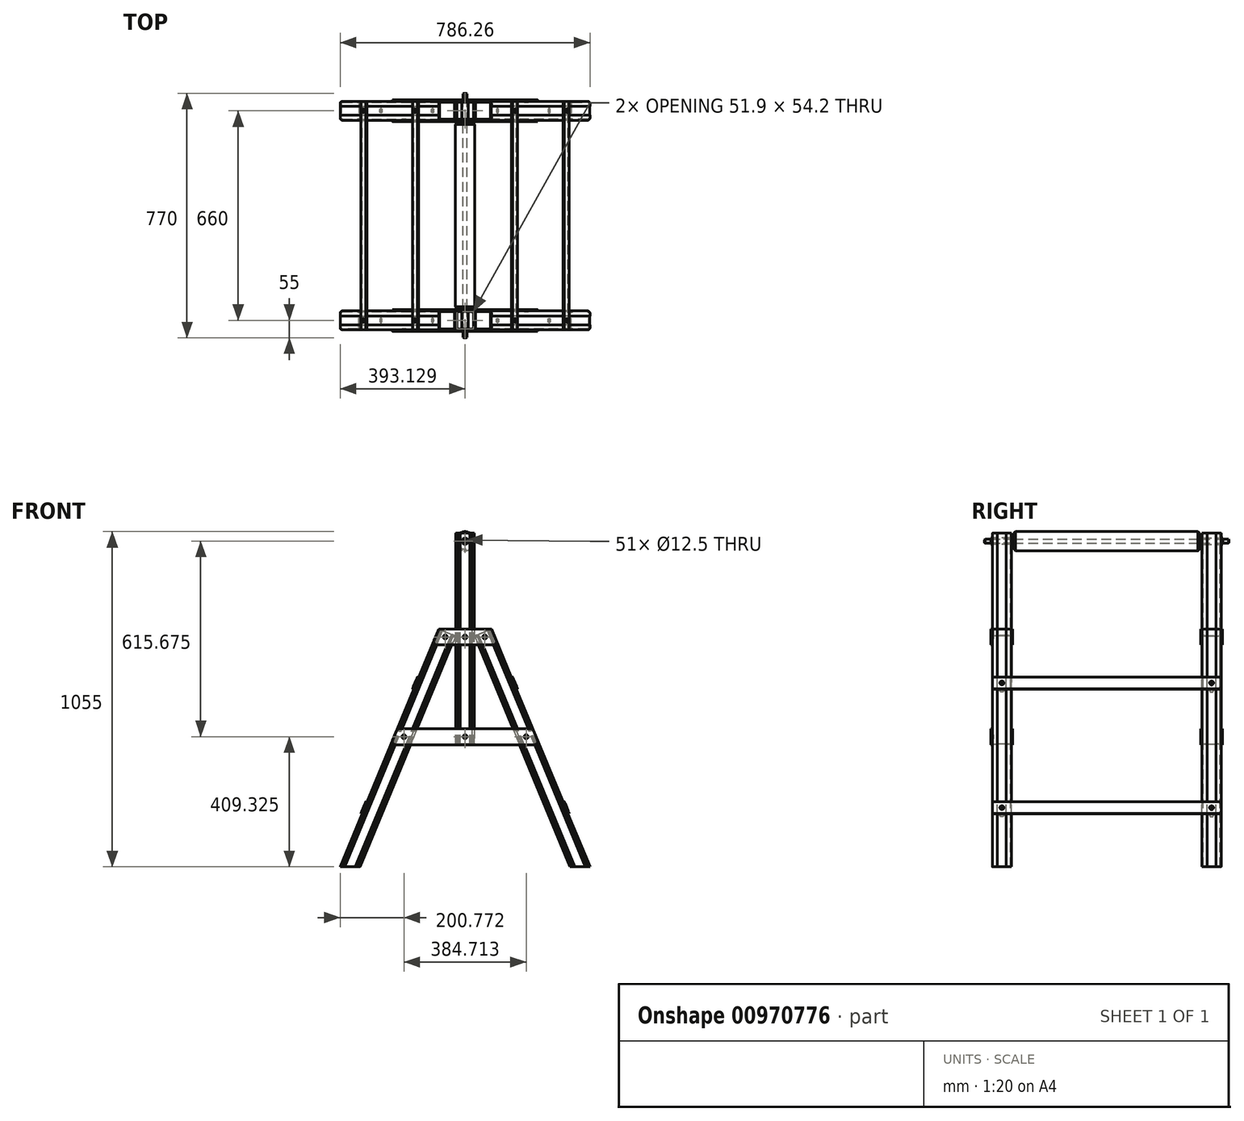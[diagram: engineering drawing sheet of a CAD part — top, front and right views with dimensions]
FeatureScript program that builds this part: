
annotation { "Feature Type Name" : "Feature", "Feature Type Description" : "" }
export const myFeature = defineFeature(function(context is Context, id is Id, definition is map)
    precondition{}
    {
        {
            var Q0;
            Q0=qCreatedBy(makeId("Front.planeOp"),FACE);
            var sketch = newSketch(context, id + "F0", { "sketchPlane" : qUnion([Q0])});
            skLineSegment(sketch, "E0", {"start": v(0, 0) * mm, "end": v(-309.97, 748.34) * mm});
            skLineSegment(sketch, "E1", {"start": v(-309.97, 748.34) * mm, "end": v(-363.28, 726.26) * mm});
            skLineSegment(sketch, "E2", {"start": v(-363.28, 726.26) * mm, "end": v(-62.45, 0) * mm});
            skLineSegment(sketch, "E3", {"start": v(-62.45, 0) * mm, "end": v(0, 0) * mm});
            skLineSegment(sketch, "E4", {"start": v(-336.63, 737.3) * mm, "end": v(-31.23, 0) * mm, "construction": true});
            skCircle(sketch, "E5", {"center": v(-330.89, 723.44) * mm, "radius": 6.25 * mm});
            skCircle(sketch, "E6", {"center": v(-200.77, 409.32) * mm, "radius": 6.25 * mm});
            skSolve(sketch);
        }
        {
            var Q0;
            Q0=qSketchRegion(id+"F0",true);
            extrude(context, id + "F1", {"entities" : qUnion([Q0]), "depth" : 60 * mm, "offsetDistance" : 25 * mm});
        }
        {
            var Q0;
            Q0=makeQuery(id+"F1.opExtrude","CAP_EDGE",EDGE,{"disambiguationData":[OSD([sQuery(id+"F0.wireOp",EDGE,"E0")])],"isStart":false});
            var Q1;
            Q1=makeQuery(id+"F1.opExtrude","CAP_EDGE",EDGE,{"disambiguationData":[OSD([sQuery(id+"F0.wireOp",EDGE,"E2")])],"isStart":false});
            var Q2;
            Q2=makeQuery(id+"F1.opExtrude","CAP_EDGE",EDGE,{"disambiguationData":[OSD([sQuery(id+"F0.wireOp",EDGE,"E0")])],"isStart":true});
            var Q3;
            Q3=makeQuery(id+"F1.opExtrude","CAP_EDGE",EDGE,{"disambiguationData":[OSD([sQuery(id+"F0.wireOp",EDGE,"E2")])],"isStart":true});
            fillet(context, id + "F2", {"entities" : qUnion([Q0, Q1, Q2, Q3]), "radius" : 7.5 * mm, "tangentPropagation" : true, "allowEdgeOverflow" : false});
        }
        {
            var Q0;
            Q0=makeQuery(id+"F1.opExtrude","SWEPT_FACE",FACE,{"disambiguationData":[OSD([sQuery(id+"F0.wireOp",EDGE,"E1")])]});
            var sketch = newSketch(context, id + "F3", { "sketchPlane" : qUnion([Q0])});
            skLineSegment(sketch, "E7", {"start": v(-50.2, -60) * mm, "end": v(-49.2, -59) * mm});
            skLineSegment(sketch, "E8", {"start": v(-49.2, -59) * mm, "end": v(-48.2, -60) * mm});
            skLineSegment(sketch, "E9", {"start": v(-48.2, -60) * mm, "end": v(-47.2, -59) * mm});
            skLineSegment(sketch, "E10", {"start": v(-47.2, -59) * mm, "end": v(-46.2, -60) * mm});
            skLineSegment(sketch, "E11", {"start": v(-46.2, -60) * mm, "end": v(-45.2, -59) * mm});
            skLineSegment(sketch, "E12", {"start": v(-45.2, -59) * mm, "end": v(-44.2, -60) * mm});
            skLineSegment(sketch, "E13", {"start": v(-28.85, -60) * mm, "end": v(-28.85, -30) * mm, "construction": true});
            skPoint(sketch, "E13.endSnap0", {"position": v(-57.7, -30) * mm});
            skLineSegment(sketch, "E14", {"start": v(-28.85, -30) * mm, "end": v(-57.7, -30) * mm, "construction": true});
            skLineSegment(sketch, "E15", {"start": v(-57.4, -44) * mm, "end": v(-57.7, -44) * mm});
            skLineSegment(sketch, "E16", {"start": v(-57.4, -44) * mm, "end": v(-57.4, -30) * mm});
            skArc(sketch, "E17.0", {"start": v(-54.8, -52.5) * mm, "mid": v(-53.45, -55.75) * mm, "end": v(-50.2, -57.1) * mm});
            skLineSegment(sketch, "E18", {"start": v(-54.8, -52.5) * mm, "end": v(-54.8, -30) * mm});
            skLineSegment(sketch, "E19", {"start": v(-50.2, -57.1) * mm, "end": v(-28.85, -57.1) * mm});
            skLineSegment(sketch, "E20.MirrorCS", {"start": v(-0.3, -44) * mm, "end": v(0, -44) * mm});
            skLineSegment(sketch, "E21.MirrorCS", {"start": v(-7.5, -60) * mm, "end": v(-8.5, -59) * mm});
            skLineSegment(sketch, "E22.MirrorCS", {"start": v(-11.5, -60) * mm, "end": v(-12.5, -59) * mm});
            skLineSegment(sketch, "E23.MirrorCS", {"start": v(-9.5, -60) * mm, "end": v(-10.5, -59) * mm});
            skLineSegment(sketch, "E24.MirrorCS", {"start": v(-12.5, -59) * mm, "end": v(-13.5, -60) * mm});
            skLineSegment(sketch, "E25.MirrorCS", {"start": v(-10.5, -59) * mm, "end": v(-11.5, -60) * mm});
            skLineSegment(sketch, "E26.MirrorCS", {"start": v(-8.5, -59) * mm, "end": v(-9.5, -60) * mm});
            skArc(sketch, "E27.MirrorCS", {"start": v(-2.9, -52.5) * mm, "mid": v(-4.25, -55.75) * mm, "end": v(-7.5, -57.1) * mm});
            skLineSegment(sketch, "E28.MirrorCS", {"start": v(-0.3, -44) * mm, "end": v(-0.3, -30) * mm});
            skLineSegment(sketch, "E29.MirrorCS", {"start": v(-7.5, -57.1) * mm, "end": v(-28.85, -57.1) * mm});
            skLineSegment(sketch, "E30.MirrorCS", {"start": v(-2.9, -52.5) * mm, "end": v(-2.9, -30) * mm});
            skLineSegment(sketch, "E31.MirrorCS", {"start": v(-50.2, 0) * mm, "end": v(-49.2, -1) * mm});
            skLineSegment(sketch, "E32.MirrorCS", {"start": v(-48.2, 0) * mm, "end": v(-47.2, -1) * mm});
            skLineSegment(sketch, "E33.MirrorCS", {"start": v(-49.2, -1) * mm, "end": v(-48.2, 0) * mm});
            skLineSegment(sketch, "E34.MirrorCS", {"start": v(-46.2, 0) * mm, "end": v(-45.2, -1) * mm});
            skLineSegment(sketch, "E35.MirrorCS", {"start": v(-47.2, -1) * mm, "end": v(-46.2, 0) * mm});
            skLineSegment(sketch, "E36.MirrorCS", {"start": v(-57.4, -16) * mm, "end": v(-57.7, -16) * mm});
            skLineSegment(sketch, "E37.MirrorCS", {"start": v(-45.2, -1) * mm, "end": v(-44.2, 0) * mm});
            skArc(sketch, "E38.MirrorCS", {"start": v(-54.8, -7.5) * mm, "mid": v(-53.45, -4.25) * mm, "end": v(-50.2, -2.9) * mm});
            skLineSegment(sketch, "E39.MirrorCS", {"start": v(-50.2, -2.9) * mm, "end": v(-28.85, -2.9) * mm});
            skLineSegment(sketch, "E40.MirrorCS", {"start": v(-54.8, -7.5) * mm, "end": v(-54.8, -30) * mm});
            skLineSegment(sketch, "E41.MirrorCS", {"start": v(-57.4, -16) * mm, "end": v(-57.4, -30) * mm});
            skLineSegment(sketch, "E42.MirrorCS", {"start": v(-9.5, 0) * mm, "end": v(-10.5, -1) * mm});
            skLineSegment(sketch, "E43.MirrorCS", {"start": v(-12.5, -1) * mm, "end": v(-13.5, 0) * mm});
            skLineSegment(sketch, "E44.MirrorCS", {"start": v(-10.5, -1) * mm, "end": v(-11.5, 0) * mm});
            skLineSegment(sketch, "E45.MirrorCS", {"start": v(-0.3, -16) * mm, "end": v(0, -16) * mm});
            skLineSegment(sketch, "E46.MirrorCS", {"start": v(-11.5, 0) * mm, "end": v(-12.5, -1) * mm});
            skLineSegment(sketch, "E47.MirrorCS", {"start": v(-7.5, 0) * mm, "end": v(-8.5, -1) * mm});
            skLineSegment(sketch, "E48.MirrorCS", {"start": v(-8.5, -1) * mm, "end": v(-9.5, 0) * mm});
            skLineSegment(sketch, "E49.MirrorCS", {"start": v(-2.9, -7.5) * mm, "end": v(-2.9, -30) * mm});
            skLineSegment(sketch, "E50.MirrorCS", {"start": v(-7.5, -2.9) * mm, "end": v(-28.85, -2.9) * mm});
            skArc(sketch, "E51.MirrorCS", {"start": v(-2.9, -7.5) * mm, "mid": v(-4.25, -4.25) * mm, "end": v(-7.5, -2.9) * mm});
            skLineSegment(sketch, "E52.MirrorCS", {"start": v(-0.3, -16) * mm, "end": v(-0.3, -30) * mm});
            skSolve(sketch);
        }
        {
            var Q0;
            Q0=makeQuery(id+"F3.imprint","IMPRINT",FACE,{"disambiguationData":[TD([[makeQuery(id+"F3.imprint","IMPRINT",EDGE,{"derivedFrom":sQuery(id+"F3.wireOp",EDGE,"E17.0")}),1.0]])]});
            var Q1;
            {var subQ0=sQuery(id+"F3.wireOp",EDGE,"E34.MirrorCS");Q1=makeQuery(id+"F3.imprint","IMPRINT",FACE,{"disambiguationData":[TD([[makeQuery(id+"F3.imprint","IMPRINT",EDGE,{"derivedFrom":subQ0}),1.0]])]});}
            var Q2;
            {var subQ0=sQuery(id+"F3.wireOp",EDGE,"E32.MirrorCS");Q2=makeQuery(id+"F3.imprint","IMPRINT",FACE,{"disambiguationData":[TD([[makeQuery(id+"F3.imprint","IMPRINT",EDGE,{"derivedFrom":subQ0}),1.0]])]});}
            var Q3;
            {var subQ0=sQuery(id+"F3.wireOp",EDGE,"E31.MirrorCS");Q3=makeQuery(id+"F3.imprint","IMPRINT",FACE,{"disambiguationData":[TD([[makeQuery(id+"F3.imprint","IMPRINT",EDGE,{"derivedFrom":subQ0}),1.0]])]});}
            var Q4;
            {var subQ1=sQuery(id+"F3.wireOp",EDGE,"E15");Q4=makeQuery(id+"F3.imprint","IMPRINT",FACE,{"disambiguationData":[TD([[makeQuery(id+"F3.imprint","IMPRINT",EDGE,{"derivedFrom":subQ1}),-1.0]])]});}
            var Q5;
            {var subQ0=sQuery(id+"F3.wireOp",EDGE,"E7");Q5=makeQuery(id+"F3.imprint","IMPRINT",FACE,{"disambiguationData":[TD([[makeQuery(id+"F3.imprint","IMPRINT",EDGE,{"derivedFrom":subQ0}),-1.0]])]});}
            var Q6;
            {var subQ0=sQuery(id+"F3.wireOp",EDGE,"E9");Q6=makeQuery(id+"F3.imprint","IMPRINT",FACE,{"disambiguationData":[TD([[makeQuery(id+"F3.imprint","IMPRINT",EDGE,{"derivedFrom":subQ0}),-1.0]])]});}
            var Q7;
            {var subQ0=sQuery(id+"F3.wireOp",EDGE,"E11");Q7=makeQuery(id+"F3.imprint","IMPRINT",FACE,{"disambiguationData":[TD([[makeQuery(id+"F3.imprint","IMPRINT",EDGE,{"derivedFrom":subQ0}),-1.0]])]});}
            var Q8;
            {var subQ0=sQuery(id+"F3.wireOp",EDGE,"E21.MirrorCS");Q8=makeQuery(id+"F3.imprint","IMPRINT",FACE,{"disambiguationData":[TD([[makeQuery(id+"F3.imprint","IMPRINT",EDGE,{"derivedFrom":subQ0}),1.0]])]});}
            var Q9;
            {var subQ0=sQuery(id+"F3.wireOp",EDGE,"E23.MirrorCS");Q9=makeQuery(id+"F3.imprint","IMPRINT",FACE,{"disambiguationData":[TD([[makeQuery(id+"F3.imprint","IMPRINT",EDGE,{"derivedFrom":subQ0}),1.0]])]});}
            var Q10;
            {var subQ0=sQuery(id+"F3.wireOp",EDGE,"E22.MirrorCS");Q10=makeQuery(id+"F3.imprint","IMPRINT",FACE,{"disambiguationData":[TD([[makeQuery(id+"F3.imprint","IMPRINT",EDGE,{"derivedFrom":subQ0}),1.0]])]});}
            var Q11;
            {var subQ1=sQuery(id+"F3.wireOp",EDGE,"E20.MirrorCS");Q11=makeQuery(id+"F3.imprint","IMPRINT",FACE,{"disambiguationData":[TD([[makeQuery(id+"F3.imprint","IMPRINT",EDGE,{"derivedFrom":subQ1}),1.0]])]});}
            var Q12;
            {var subQ0=sQuery(id+"F3.wireOp",EDGE,"E47.MirrorCS");Q12=makeQuery(id+"F3.imprint","IMPRINT",FACE,{"disambiguationData":[TD([[makeQuery(id+"F3.imprint","IMPRINT",EDGE,{"derivedFrom":subQ0}),-1.0]])]});}
            var Q13;
            {var subQ0=sQuery(id+"F3.wireOp",EDGE,"E42.MirrorCS");Q13=makeQuery(id+"F3.imprint","IMPRINT",FACE,{"disambiguationData":[TD([[makeQuery(id+"F3.imprint","IMPRINT",EDGE,{"derivedFrom":subQ0}),-1.0]])]});}
            var Q14;
            {var subQ0=sQuery(id+"F3.wireOp",EDGE,"E43.MirrorCS");Q14=makeQuery(id+"F3.imprint","IMPRINT",FACE,{"disambiguationData":[TD([[makeQuery(id+"F3.imprint","IMPRINT",EDGE,{"derivedFrom":subQ0}),-1.0]])]});}
            var Q15;
            Q15=makeQuery(id+"F1.opExtrude","SWEPT_FACE",FACE,{"disambiguationData":[OSD([sQuery(id+"F0.wireOp",EDGE,"E3")])]});
            extrude(context, id + "F4", {"entities" : qUnion([Q0, Q1, Q2, Q3, Q4, Q5, Q6, Q7, Q8, Q9, Q10, Q11, Q12, Q13, Q14]), "operationType" : NewBodyOperationType.REMOVE, "endBound" : BoundingType.UP_TO_SURFACE, "oppositeDirection" : true, "depth" : 25 * mm, "endBoundEntityFace" : qUnion([Q15]), "offsetDistance" : 25 * mm});
        }
        {
            var Q0;
            {var subQ0=sQuery(id+"F0.wireOp",EDGE,"E0");Q0=makeQuery(id+"F4.boolean.opBoolean","SPLIT",FACE,{"disambiguationData":[TD([makeQuery(id+"F4.opExtrude","SWEPT_FACE",FACE,{"disambiguationData":[OSD([sQuery(id+"F3.wireOp",EDGE,"E20.MirrorCS")])]})])],"derivedFrom":makeQuery(id+"F1.opExtrude","SWEPT_FACE",FACE,{"disambiguationData":[OSD([subQ0])]})});}
            var sketch = newSketch(context, id + "F5", { "sketchPlane" : qUnion([Q0])});
            skLineSegment(sketch, "E53", {"start": v(-60, 0) * mm, "end": v(0, 0) * mm, "construction": true});
            skLineSegment(sketch, "E54", {"start": v(-30, 0) * mm, "end": v(-30, 810) * mm, "construction": true});
            skCircle(sketch, "E55", {"center": v(-30, 200) * mm, "radius": 6.25 * mm});
            skCircle(sketch, "E56", {"center": v(-30, 625) * mm, "radius": 6.25 * mm});
            skSolve(sketch);
        }
        {
            var Q0;
            Q0=qSketchRegion(id+"F5",true);
            var Q1;
            {var subQ0=sQuery(id+"F0.wireOp",EDGE,"E2");Q1=makeQuery(id+"F4.boolean.opBoolean","SPLIT",FACE,{"disambiguationData":[TD([makeQuery(id+"F4.opExtrude","SWEPT_FACE",FACE,{"disambiguationData":[OSD([sQuery(id+"F3.wireOp",EDGE,"E15")])]})])],"derivedFrom":makeQuery(id+"F1.opExtrude","SWEPT_FACE",FACE,{"disambiguationData":[OSD([subQ0])]})});}
            extrude(context, id + "F6", {"entities" : qUnion([Q0]), "operationType" : NewBodyOperationType.REMOVE, "endBound" : BoundingType.UP_TO_SURFACE, "oppositeDirection" : true, "depth" : 25 * mm, "endBoundEntityFace" : qUnion([Q1]), "offsetDistance" : 25 * mm});
        }
        {
            var Q0;
            Q0=makeQuery(id+"F1.opExtrude","CAP_FACE",FACE,{"disambiguationData":[OSD([sQuery(id+"F0.wireOp",EDGE,"E0"),sQuery(id+"F0.wireOp",EDGE,"E1"),sQuery(id+"F0.wireOp",EDGE,"E2"),sQuery(id+"F0.wireOp",EDGE,"E3")])],"isStart":false});
            var sketch = newSketch(context, id + "F7", { "sketchPlane" : qUnion([Q0])});
            skLineSegment(sketch, "E57", {"start": v(-364.28, 1050) * mm, "end": v(-364.28, 386) * mm});
            skLineSegment(sketch, "E58", {"start": v(-364.28, 386) * mm, "end": v(-421.98, 386) * mm});
            skLineSegment(sketch, "E59", {"start": v(-421.98, 386) * mm, "end": v(-421.98, 1050) * mm});
            skLineSegment(sketch, "E60", {"start": v(-421.98, 1050) * mm, "end": v(-364.28, 1050) * mm});
            skLineSegment(sketch, "E61", {"start": v(-393.13, 386) * mm, "end": v(-393.13, 1050) * mm, "construction": true});
            skCircle(sketch, "E62", {"center": v(-393.13, 723.44) * mm, "radius": 6.25 * mm});
            skCircle(sketch, "E63", {"center": v(-393.13, 409.32) * mm, "radius": 6.25 * mm});
            skCircle(sketch, "E64", {"center": v(-393.13, 1025) * mm, "radius": 10 * mm});
            skLineSegment(sketch, "E65", {"start": v(-569.02, 403.07) * mm, "end": v(-237.44, 403.07) * mm, "construction": true});
            skLineSegment(sketch, "E66", {"start": v(-572.05, 717.2) * mm, "end": v(-0.55, 717.2) * mm, "construction": true});
            skSolve(sketch);
        }
        {
            var Q0;
            Q0=qSketchRegion(id+"F7",true);
            extrude(context, id + "F8", {"entities" : qUnion([Q0]), "oppositeDirection" : true, "depth" : 60 * mm, "offsetDistance" : 25 * mm});
        }
        {
            var Q0;
            Q0=makeQuery(id+"F8.opExtrude","CAP_EDGE",EDGE,{"disambiguationData":[OSD([sQuery(id+"F7.wireOp",EDGE,"E59")])],"isStart":true});
            var Q1;
            Q1=makeQuery(id+"F8.opExtrude","CAP_EDGE",EDGE,{"disambiguationData":[OSD([sQuery(id+"F7.wireOp",EDGE,"E57")])],"isStart":true});
            var Q2;
            Q2=makeQuery(id+"F8.opExtrude","CAP_EDGE",EDGE,{"disambiguationData":[OSD([sQuery(id+"F7.wireOp",EDGE,"E57")])],"isStart":false});
            var Q3;
            Q3=makeQuery(id+"F8.opExtrude","CAP_EDGE",EDGE,{"disambiguationData":[OSD([sQuery(id+"F7.wireOp",EDGE,"E59")])],"isStart":false});
            fillet(context, id + "F9", {"entities" : qUnion([Q0, Q1, Q2, Q3]), "radius" : 7.5 * mm, "tangentPropagation" : true, "allowEdgeOverflow" : false});
        }
        {
            var Q0;
            Q0=makeQuery(id+"F8.opExtrude","SWEPT_FACE",FACE,{"disambiguationData":[OSD([sQuery(id+"F7.wireOp",EDGE,"E60")])]});
            var sketch = newSketch(context, id + "F10", { "sketchPlane" : qUnion([Q0])});
            skLineSegment(sketch, "E67", {"start": v(-421.98, -30) * mm, "end": v(-393.13, -30) * mm, "construction": true});
            skPoint(sketch, "E67.endSnap0", {"position": v(-393.13, -60) * mm});
            skLineSegment(sketch, "E68", {"start": v(-393.13, -30) * mm, "end": v(-393.13, -60) * mm, "construction": true});
            skLineSegment(sketch, "E69", {"start": v(-414.48, -60) * mm, "end": v(-413.48, -59) * mm});
            skLineSegment(sketch, "E70", {"start": v(-413.48, -59) * mm, "end": v(-412.48, -60) * mm});
            skLineSegment(sketch, "E71", {"start": v(-421.68, -30) * mm, "end": v(-421.68, -44) * mm});
            skLineSegment(sketch, "E72", {"start": v(-421.68, -44) * mm, "end": v(-421.98, -44) * mm});
            skLineSegment(sketch, "E73", {"start": v(-412.48, -60) * mm, "end": v(-411.48, -59) * mm});
            skLineSegment(sketch, "E74", {"start": v(-411.48, -59) * mm, "end": v(-410.48, -60) * mm});
            skLineSegment(sketch, "E75", {"start": v(-410.48, -60) * mm, "end": v(-409.48, -59) * mm});
            skLineSegment(sketch, "E76", {"start": v(-409.48, -59) * mm, "end": v(-408.48, -60) * mm});
            skArc(sketch, "E77.0", {"start": v(-419.08, -52.5) * mm, "mid": v(-417.73, -55.75) * mm, "end": v(-414.48, -57.1) * mm});
            skLineSegment(sketch, "E78", {"start": v(-419.08, -52.5) * mm, "end": v(-419.08, -30) * mm});
            skLineSegment(sketch, "E79", {"start": v(-414.48, -57.1) * mm, "end": v(-393.13, -57.1) * mm});
            skLineSegment(sketch, "E80.MirrorCS", {"start": v(-364.58, -44) * mm, "end": v(-364.28, -44) * mm});
            skLineSegment(sketch, "E81.MirrorCS", {"start": v(-371.78, -60) * mm, "end": v(-372.78, -59) * mm});
            skLineSegment(sketch, "E82.MirrorCS", {"start": v(-372.78, -59) * mm, "end": v(-373.78, -60) * mm});
            skLineSegment(sketch, "E83.MirrorCS", {"start": v(-376.78, -59) * mm, "end": v(-377.78, -60) * mm});
            skLineSegment(sketch, "E84.MirrorCS", {"start": v(-373.78, -60) * mm, "end": v(-374.78, -59) * mm});
            skLineSegment(sketch, "E85.MirrorCS", {"start": v(-374.78, -59) * mm, "end": v(-375.78, -60) * mm});
            skLineSegment(sketch, "E86.MirrorCS", {"start": v(-375.78, -60) * mm, "end": v(-376.78, -59) * mm});
            skArc(sketch, "E87.MirrorCS", {"start": v(-367.18, -52.5) * mm, "mid": v(-368.53, -55.75) * mm, "end": v(-371.78, -57.1) * mm});
            skLineSegment(sketch, "E88.MirrorCS", {"start": v(-364.58, -30) * mm, "end": v(-364.58, -44) * mm});
            skLineSegment(sketch, "E89.MirrorCS", {"start": v(-371.78, -57.1) * mm, "end": v(-393.13, -57.1) * mm});
            skLineSegment(sketch, "E90.MirrorCS", {"start": v(-367.18, -52.5) * mm, "end": v(-367.18, -30) * mm});
            skLineSegment(sketch, "E91.MirrorCS", {"start": v(-412.48, 0) * mm, "end": v(-411.48, -1) * mm});
            skLineSegment(sketch, "E92.MirrorCS", {"start": v(-414.48, 0) * mm, "end": v(-413.48, -1) * mm});
            skLineSegment(sketch, "E93.MirrorCS", {"start": v(-413.48, -1) * mm, "end": v(-412.48, 0) * mm});
            skLineSegment(sketch, "E94.MirrorCS", {"start": v(-411.48, -1) * mm, "end": v(-410.48, 0) * mm});
            skLineSegment(sketch, "E95.MirrorCS", {"start": v(-421.68, -16) * mm, "end": v(-421.98, -16) * mm});
            skLineSegment(sketch, "E96.MirrorCS", {"start": v(-410.48, 0) * mm, "end": v(-409.48, -1) * mm});
            skLineSegment(sketch, "E97.MirrorCS", {"start": v(-409.48, -1) * mm, "end": v(-408.48, 0) * mm});
            skArc(sketch, "E98.MirrorCS", {"start": v(-419.08, -7.5) * mm, "mid": v(-417.73, -4.25) * mm, "end": v(-414.48, -2.9) * mm});
            skLineSegment(sketch, "E99.MirrorCS", {"start": v(-414.48, -2.9) * mm, "end": v(-393.13, -2.9) * mm});
            skLineSegment(sketch, "E100.MirrorCS", {"start": v(-419.08, -7.5) * mm, "end": v(-419.08, -30) * mm});
            skLineSegment(sketch, "E101.MirrorCS", {"start": v(-421.68, -30) * mm, "end": v(-421.68, -16) * mm});
            skLineSegment(sketch, "E102.MirrorCS", {"start": v(-374.78, -1) * mm, "end": v(-375.78, 0) * mm});
            skLineSegment(sketch, "E103.MirrorCS", {"start": v(-375.78, 0) * mm, "end": v(-376.78, -1) * mm});
            skLineSegment(sketch, "E104.MirrorCS", {"start": v(-371.78, 0) * mm, "end": v(-372.78, -1) * mm});
            skLineSegment(sketch, "E105.MirrorCS", {"start": v(-372.78, -1) * mm, "end": v(-373.78, 0) * mm});
            skLineSegment(sketch, "E106.MirrorCS", {"start": v(-373.78, 0) * mm, "end": v(-374.78, -1) * mm});
            skLineSegment(sketch, "E107.MirrorCS", {"start": v(-364.58, -16) * mm, "end": v(-364.28, -16) * mm});
            skLineSegment(sketch, "E108.MirrorCS", {"start": v(-376.78, -1) * mm, "end": v(-377.78, 0) * mm});
            skArc(sketch, "E109.MirrorCS", {"start": v(-367.18, -7.5) * mm, "mid": v(-368.53, -4.25) * mm, "end": v(-371.78, -2.9) * mm});
            skLineSegment(sketch, "E110.MirrorCS", {"start": v(-364.58, -30) * mm, "end": v(-364.58, -16) * mm});
            skLineSegment(sketch, "E111.MirrorCS", {"start": v(-367.18, -7.5) * mm, "end": v(-367.18, -30) * mm});
            skLineSegment(sketch, "E112.MirrorCS", {"start": v(-371.78, -2.9) * mm, "end": v(-393.13, -2.9) * mm});
            skSolve(sketch);
        }
        {
            var Q0;
            {var subQ0=sQuery(id+"F10.wireOp",EDGE,"E69");Q0=makeQuery(id+"F10.imprint","IMPRINT",FACE,{"disambiguationData":[TD([[makeQuery(id+"F10.imprint","IMPRINT",EDGE,{"derivedFrom":subQ0}),-1.0]])]});}
            var Q1;
            {var subQ0=sQuery(id+"F10.wireOp",EDGE,"E73");Q1=makeQuery(id+"F10.imprint","IMPRINT",FACE,{"disambiguationData":[TD([[makeQuery(id+"F10.imprint","IMPRINT",EDGE,{"derivedFrom":subQ0}),-1.0]])]});}
            var Q2;
            {var subQ0=sQuery(id+"F10.wireOp",EDGE,"E75");Q2=makeQuery(id+"F10.imprint","IMPRINT",FACE,{"disambiguationData":[TD([[makeQuery(id+"F10.imprint","IMPRINT",EDGE,{"derivedFrom":subQ0}),-1.0]])]});}
            var Q3;
            {var subQ0=sQuery(id+"F10.wireOp",EDGE,"E83.MirrorCS");Q3=makeQuery(id+"F10.imprint","IMPRINT",FACE,{"disambiguationData":[TD([[makeQuery(id+"F10.imprint","IMPRINT",EDGE,{"derivedFrom":subQ0}),1.0]])]});}
            var Q4;
            {var subQ0=sQuery(id+"F10.wireOp",EDGE,"E84.MirrorCS");Q4=makeQuery(id+"F10.imprint","IMPRINT",FACE,{"disambiguationData":[TD([[makeQuery(id+"F10.imprint","IMPRINT",EDGE,{"derivedFrom":subQ0}),1.0]])]});}
            var Q5;
            {var subQ0=sQuery(id+"F10.wireOp",EDGE,"E81.MirrorCS");Q5=makeQuery(id+"F10.imprint","IMPRINT",FACE,{"disambiguationData":[TD([[makeQuery(id+"F10.imprint","IMPRINT",EDGE,{"derivedFrom":subQ0}),1.0]])]});}
            var Q6;
            Q6=makeQuery(id+"F10.imprint","IMPRINT",FACE,{"disambiguationData":[TD([[makeQuery(id+"F10.imprint","IMPRINT",EDGE,{"derivedFrom":sQuery(id+"F10.wireOp",EDGE,"E71")}),-1.0]])]});
            var Q7;
            {var subQ1=sQuery(id+"F10.wireOp",EDGE,"E80.MirrorCS");Q7=makeQuery(id+"F10.imprint","IMPRINT",FACE,{"disambiguationData":[TD([[makeQuery(id+"F10.imprint","IMPRINT",EDGE,{"derivedFrom":subQ1}),1.0]])]});}
            var Q8;
            {var subQ0=sQuery(id+"F10.wireOp",EDGE,"E103.MirrorCS");Q8=makeQuery(id+"F10.imprint","IMPRINT",FACE,{"disambiguationData":[TD([[makeQuery(id+"F10.imprint","IMPRINT",EDGE,{"derivedFrom":subQ0}),-1.0]])]});}
            var Q9;
            {var subQ0=sQuery(id+"F10.wireOp",EDGE,"E102.MirrorCS");Q9=makeQuery(id+"F10.imprint","IMPRINT",FACE,{"disambiguationData":[TD([[makeQuery(id+"F10.imprint","IMPRINT",EDGE,{"derivedFrom":subQ0}),-1.0]])]});}
            var Q10;
            {var subQ0=sQuery(id+"F10.wireOp",EDGE,"E104.MirrorCS");Q10=makeQuery(id+"F10.imprint","IMPRINT",FACE,{"disambiguationData":[TD([[makeQuery(id+"F10.imprint","IMPRINT",EDGE,{"derivedFrom":subQ0}),-1.0]])]});}
            var Q11;
            {var subQ0=sQuery(id+"F10.wireOp",EDGE,"E92.MirrorCS");Q11=makeQuery(id+"F10.imprint","IMPRINT",FACE,{"disambiguationData":[TD([[makeQuery(id+"F10.imprint","IMPRINT",EDGE,{"derivedFrom":subQ0}),1.0]])]});}
            var Q12;
            {var subQ0=sQuery(id+"F10.wireOp",EDGE,"E91.MirrorCS");Q12=makeQuery(id+"F10.imprint","IMPRINT",FACE,{"disambiguationData":[TD([[makeQuery(id+"F10.imprint","IMPRINT",EDGE,{"derivedFrom":subQ0}),1.0]])]});}
            var Q13;
            {var subQ0=sQuery(id+"F10.wireOp",EDGE,"E96.MirrorCS");Q13=makeQuery(id+"F10.imprint","IMPRINT",FACE,{"disambiguationData":[TD([[makeQuery(id+"F10.imprint","IMPRINT",EDGE,{"derivedFrom":subQ0}),1.0]])]});}
            var Q14;
            Q14=makeQuery(id+"F10.imprint","IMPRINT",FACE,{"disambiguationData":[TD([[makeQuery(id+"F10.imprint","IMPRINT",EDGE,{"derivedFrom":sQuery(id+"F10.wireOp",EDGE,"E77.0")}),1.0]])]});
            var Q15;
            Q15=makeQuery(id+"F8.opExtrude","SWEPT_FACE",FACE,{"disambiguationData":[OSD([sQuery(id+"F7.wireOp",EDGE,"E58")])]});
            extrude(context, id + "F11", {"entities" : qUnion([Q0, Q1, Q2, Q3, Q4, Q5, Q6, Q7, Q8, Q9, Q10, Q11, Q12, Q13, Q14]), "operationType" : NewBodyOperationType.REMOVE, "endBound" : BoundingType.UP_TO_SURFACE, "oppositeDirection" : true, "depth" : 25 * mm, "endBoundEntityFace" : qUnion([Q15]), "offsetDistance" : 25 * mm});
        }
        {
            var Q0;
            Q0=makeQuery(id+"F11.boolean.opBoolean","COPY",FACE,{"derivedFrom":makeQuery(id+"F11.opExtrude","SWEPT_FACE",FACE,{"disambiguationData":[OSD([sQuery(id+"F10.wireOp",EDGE,"E88.MirrorCS"),sQuery(id+"F10.wireOp",EDGE,"E110.MirrorCS")])]})});
            var Q1;
            Q1=makeQuery(id+"F11.boolean.opBoolean","COPY",FACE,{"derivedFrom":makeQuery(id+"F11.opExtrude","SWEPT_FACE",FACE,{"disambiguationData":[OSD([sQuery(id+"F10.wireOp",EDGE,"E71"),sQuery(id+"F10.wireOp",EDGE,"E101.MirrorCS")])]})});
            cPlane(context, id + "F12", {"entities" : qUnion([Q0, Q1]), "cplaneType" : CPlaneType.MID_PLANE, "offset" : 25 * mm, "width" : 150 * mm, "height" : 150 * mm});
        }
        {
            var Q0;
            Q0=makeQuery(id+"F1.opExtrude","SWEPT_BODY",BODY,{"disambiguationData":[OSD([sQuery(id+"F0.wireOp",EDGE,"E0"),sQuery(id+"F0.wireOp",EDGE,"E1"),sQuery(id+"F0.wireOp",EDGE,"E2"),sQuery(id+"F0.wireOp",EDGE,"E3")])]});
            var Q1;
            Q1=qCreatedBy(id+"F12.planeOp",FACE);
            mirror(context, id + "F13", {"entities" : qUnion([Q0]), "mirrorPlane" : qUnion([Q1])});
        }
        {
            var Q0;
            Q0=makeQuery(id+"F13.opPattern","COPY",FACE,{"derivedFrom":makeQuery(id+"F1.opExtrude","CAP_FACE",FACE,{"disambiguationData":[OSD([sQuery(id+"F0.wireOp",EDGE,"E0"),sQuery(id+"F0.wireOp",EDGE,"E1"),sQuery(id+"F0.wireOp",EDGE,"E2"),sQuery(id+"F0.wireOp",EDGE,"E3")])],"isStart":false}),"instanceName":"1"});
            var sketch = newSketch(context, id + "F14", { "sketchPlane" : qUnion([Q0])});
            skCircle(sketch, "E113", {"center": v(-393.13, 723.44) * mm, "radius": 6.25 * mm});
            skCircle(sketch, "E114", {"center": v(-455.38, 723.44) * mm, "radius": 6.25 * mm});
            skCircle(sketch, "E115", {"center": v(-330.89, 723.44) * mm, "radius": 6.25 * mm});
            skLineSegment(sketch, "E116", {"start": v(-455.38, 723.44) * mm, "end": v(-330.89, 723.44) * mm, "construction": true});
            skLineSegment(sketch, "E117", {"start": v(-476.25, 748.44) * mm, "end": v(-496.96, 698.44) * mm});
            skLineSegment(sketch, "E118", {"start": v(-496.96, 698.44) * mm, "end": v(-289.3, 698.44) * mm});
            skLineSegment(sketch, "E119", {"start": v(-289.3, 698.44) * mm, "end": v(-310.02, 748.44) * mm});
            skLineSegment(sketch, "E120", {"start": v(-310.02, 748.44) * mm, "end": v(-476.25, 748.44) * mm});
            skLineSegment(sketch, "E121", {"start": v(-393.13, 723.44) * mm, "end": v(-393.13, 748.44) * mm, "construction": true});
            skLineSegment(sketch, "E122", {"start": v(-393.13, 723.44) * mm, "end": v(-393.13, 698.44) * mm, "construction": true});
            skCircle(sketch, "E123", {"center": v(-585.49, 409.32) * mm, "radius": 6.25 * mm});
            skCircle(sketch, "E124", {"center": v(-393.13, 409.32) * mm, "radius": 6.25 * mm});
            skCircle(sketch, "E125", {"center": v(-200.77, 409.32) * mm, "radius": 6.25 * mm});
            skLineSegment(sketch, "E126", {"start": v(-606.36, 434.32) * mm, "end": v(-627.07, 384.32) * mm});
            skLineSegment(sketch, "E127", {"start": v(-627.07, 384.32) * mm, "end": v(-159.2, 384.32) * mm});
            skLineSegment(sketch, "E128", {"start": v(-159.2, 384.32) * mm, "end": v(-179.9, 434.32) * mm});
            skLineSegment(sketch, "E129", {"start": v(-179.9, 434.32) * mm, "end": v(-606.36, 434.32) * mm});
            skLineSegment(sketch, "E130", {"start": v(-585.49, 409.32) * mm, "end": v(-200.77, 409.32) * mm, "construction": true});
            skLineSegment(sketch, "E131", {"start": v(-393.13, 409.32) * mm, "end": v(-393.13, 384.32) * mm, "construction": true});
            skLineSegment(sketch, "E132", {"start": v(-393.13, 409.32) * mm, "end": v(-393.13, 434.32) * mm, "construction": true});
            skSolve(sketch);
        }
        {
            var Q0;
            Q0=qSketchRegion(id+"F14",true);
            extrude(context, id + "F15", {"entities" : qUnion([Q0]), "depth" : 4 * mm, "offsetDistance" : 25 * mm});
        }
        {
            var Q0;
            Q0=makeQuery(id+"F15.opExtrude","SWEPT_EDGE",EDGE,{"disambiguationData":[OSD([sQuery(id+"F14.wireOp",EDGE,"E119"),sQuery(id+"F14.wireOp",EDGE,"E120")])]});
            var Q1;
            Q1=makeQuery(id+"F15.opExtrude","SWEPT_EDGE",EDGE,{"disambiguationData":[OSD([sQuery(id+"F14.wireOp",EDGE,"E118"),sQuery(id+"F14.wireOp",EDGE,"E119")])]});
            var Q2;
            Q2=makeQuery(id+"F15.opExtrude","SWEPT_EDGE",EDGE,{"disambiguationData":[OSD([sQuery(id+"F14.wireOp",EDGE,"E117"),sQuery(id+"F14.wireOp",EDGE,"E118")])]});
            var Q3;
            Q3=makeQuery(id+"F15.opExtrude","SWEPT_EDGE",EDGE,{"disambiguationData":[OSD([sQuery(id+"F14.wireOp",EDGE,"E117"),sQuery(id+"F14.wireOp",EDGE,"E120")])]});
            var Q4;
            Q4=makeQuery(id+"F15.opExtrude","SWEPT_EDGE",EDGE,{"disambiguationData":[OSD([sQuery(id+"F14.wireOp",EDGE,"E126"),sQuery(id+"F14.wireOp",EDGE,"E127")])]});
            var Q5;
            Q5=makeQuery(id+"F15.opExtrude","SWEPT_EDGE",EDGE,{"disambiguationData":[OSD([sQuery(id+"F14.wireOp",EDGE,"E126"),sQuery(id+"F14.wireOp",EDGE,"E129")])]});
            var Q6;
            Q6=makeQuery(id+"F15.opExtrude","SWEPT_EDGE",EDGE,{"disambiguationData":[OSD([sQuery(id+"F14.wireOp",EDGE,"E128"),sQuery(id+"F14.wireOp",EDGE,"E129")])]});
            var Q7;
            Q7=makeQuery(id+"F15.opExtrude","SWEPT_EDGE",EDGE,{"disambiguationData":[OSD([sQuery(id+"F14.wireOp",EDGE,"E127"),sQuery(id+"F14.wireOp",EDGE,"E128")])]});
            fillet(context, id + "F16", {"entities" : qUnion([Q0, Q1, Q2, Q3, Q4, Q5, Q6, Q7]), "radius" : 10 * mm, "tangentPropagation" : true, "allowEdgeOverflow" : false});
        }
        {
            var Q0;
            Q0=makeQuery(id+"F11.boolean.opBoolean","COPY",FACE,{"derivedFrom":makeQuery(id+"F11.opExtrude","SWEPT_FACE",FACE,{"disambiguationData":[OSD([sQuery(id+"F10.wireOp",EDGE,"E99.MirrorCS"),sQuery(id+"F10.wireOp",EDGE,"E112.MirrorCS")])]})});
            var Q1;
            Q1=makeQuery(id+"F11.boolean.opBoolean","COPY",FACE,{"derivedFrom":makeQuery(id+"F11.opExtrude","SWEPT_FACE",FACE,{"disambiguationData":[OSD([sQuery(id+"F10.wireOp",EDGE,"E79"),sQuery(id+"F10.wireOp",EDGE,"E89.MirrorCS")])]})});
            cPlane(context, id + "F17", {"entities" : qUnion([Q0, Q1]), "cplaneType" : CPlaneType.MID_PLANE, "offset" : 25 * mm, "width" : 150 * mm, "height" : 150 * mm});
        }
        {
            var Q0;
            Q0=makeQuery(id+"F15.opExtrude","SWEPT_BODY",BODY,{"disambiguationData":[OSD([sQuery(id+"F14.wireOp",EDGE,"AObNcfa6-3aEB-Q23v-DqTa-hHXQzILQL1yk"),sQuery(id+"F14.wireOp",EDGE,"kQLOXQbJ-7LkH-e0s8-5nGH-8ApHq5aegqA2"),sQuery(id+"F14.wireOp",EDGE,"sbUFB5Ax-OFtd-hsSn-JXOX-JtcZg7yGTbC4"),sQuery(id+"F14.wireOp",EDGE,"prO6f2mF-Cr0M-C9lJ-yZKx-Iy5yvvu78a9a"),sQuery(id+"F14.wireOp",EDGE,"E113"),sQuery(id+"F14.wireOp",EDGE,"E114"),sQuery(id+"F14.wireOp",EDGE,"E115")])]});
            var Q1;
            Q1=makeQuery(id+"F15.opExtrude","SWEPT_BODY",BODY,{"disambiguationData":[OSD([sQuery(id+"F14.wireOp",EDGE,"E123"),sQuery(id+"F14.wireOp",EDGE,"E124"),sQuery(id+"F14.wireOp",EDGE,"E125"),sQuery(id+"F14.wireOp",EDGE,"E126"),sQuery(id+"F14.wireOp",EDGE,"E127"),sQuery(id+"F14.wireOp",EDGE,"E128"),sQuery(id+"F14.wireOp",EDGE,"E129")])]});
            var Q2;
            Q2=qCreatedBy(id+"F17.planeOp",FACE);
            mirror(context, id + "F18", {"entities" : qUnion([Q0, Q1]), "mirrorPlane" : qUnion([Q2])});
        }
        {
            var Q0;
            Q0=makeQuery(id+"F8.opExtrude","CAP_FACE",FACE,{"disambiguationData":[OSD([sQuery(id+"F7.wireOp",EDGE,"E57"),sQuery(id+"F7.wireOp",EDGE,"E58"),sQuery(id+"F7.wireOp",EDGE,"E59"),sQuery(id+"F7.wireOp",EDGE,"E60"),sQuery(id+"F7.wireOp",EDGE,"E62"),sQuery(id+"F7.wireOp",EDGE,"E63"),sQuery(id+"F7.wireOp",EDGE,"E64")])],"isStart":true});
            cPlane(context, id + "F19", {"entities" : qUnion([Q0]), "cplaneType" : CPlaneType.OFFSET, "offset" : 300 * mm, "width" : 150 * mm, "height" : 150 * mm});
        }
        {
            var Q0;
            Q0=qCreatedBy(id+"F17.planeOp",FACE);
            var sketch = newSketch(context, id + "F20", { "sketchPlane" : qUnion([Q0])});
            skCircle(sketch, "E133", {"center": v(-393.13, 1025) * mm, "radius": 6.25 * mm});
            skCircle(sketch, "E134", {"center": v(-393.13, 1025) * mm, "radius": 10 * mm});
            skSolve(sketch);
        }
        {
            var Q0;
            Q0 = qSketchRegion(id + "F20", true);
            extrude(context, id + "F21", {"entities" : qUnion([Q0]), "endBound" : BoundingType.SYMMETRIC, "depth" : 70 * mm, "offsetDistance" : 25 * mm});
        }
        {
            var Q0;
            Q0=makeQuery(id+"F1.opExtrude","SWEPT_BODY",BODY,{"disambiguationData":[OSD([sQuery(id+"F0.wireOp",EDGE,"E0"),sQuery(id+"F0.wireOp",EDGE,"E1"),sQuery(id+"F0.wireOp",EDGE,"E2"),sQuery(id+"F0.wireOp",EDGE,"E3"),sQuery(id+"F0.wireOp",EDGE,"E5"),sQuery(id+"F0.wireOp",EDGE,"E6")])]});
            var Q1;
            Q1=makeQuery(id+"F8.opExtrude","SWEPT_BODY",BODY,{"disambiguationData":[OSD([sQuery(id+"F7.wireOp",EDGE,"E57"),sQuery(id+"F7.wireOp",EDGE,"E58"),sQuery(id+"F7.wireOp",EDGE,"E59"),sQuery(id+"F7.wireOp",EDGE,"E60"),sQuery(id+"F7.wireOp",EDGE,"E62"),sQuery(id+"F7.wireOp",EDGE,"E63"),sQuery(id+"F7.wireOp",EDGE,"E64")])]});
            var Q2;
            Q2=makeQuery(id+"F13.opPattern","COPY",BODY,{"derivedFrom":makeQuery(id+"F1.opExtrude","SWEPT_BODY",BODY,{"disambiguationData":[OSD([sQuery(id+"F0.wireOp",EDGE,"E0"),sQuery(id+"F0.wireOp",EDGE,"E1"),sQuery(id+"F0.wireOp",EDGE,"E2"),sQuery(id+"F0.wireOp",EDGE,"E3"),sQuery(id+"F0.wireOp",EDGE,"E5"),sQuery(id+"F0.wireOp",EDGE,"E6")])]}),"instanceName":"1"});
            var Q3;
            Q3=makeQuery(id+"F15.opExtrude","SWEPT_BODY",BODY,{"disambiguationData":[OSD([sQuery(id+"F14.wireOp",EDGE,"E113"),sQuery(id+"F14.wireOp",EDGE,"E114"),sQuery(id+"F14.wireOp",EDGE,"E115"),sQuery(id+"F14.wireOp",EDGE,"E117"),sQuery(id+"F14.wireOp",EDGE,"E118"),sQuery(id+"F14.wireOp",EDGE,"E119"),sQuery(id+"F14.wireOp",EDGE,"E120")])]});
            var Q4;
            Q4=makeQuery(id+"F15.opExtrude","SWEPT_BODY",BODY,{"disambiguationData":[OSD([sQuery(id+"F14.wireOp",EDGE,"E123"),sQuery(id+"F14.wireOp",EDGE,"E124"),sQuery(id+"F14.wireOp",EDGE,"E125"),sQuery(id+"F14.wireOp",EDGE,"E126"),sQuery(id+"F14.wireOp",EDGE,"E127"),sQuery(id+"F14.wireOp",EDGE,"E128"),sQuery(id+"F14.wireOp",EDGE,"E129")])]});
            var Q5;
            Q5=makeQuery(id+"F18.opPattern","COPY",BODY,{"derivedFrom":makeQuery(id+"F15.opExtrude","SWEPT_BODY",BODY,{"disambiguationData":[OSD([sQuery(id+"F14.wireOp",EDGE,"E113"),sQuery(id+"F14.wireOp",EDGE,"E114"),sQuery(id+"F14.wireOp",EDGE,"E115"),sQuery(id+"F14.wireOp",EDGE,"E117"),sQuery(id+"F14.wireOp",EDGE,"E118"),sQuery(id+"F14.wireOp",EDGE,"E119"),sQuery(id+"F14.wireOp",EDGE,"E120")])]}),"instanceName":"1"});
            var Q6;
            Q6=makeQuery(id+"F18.opPattern","COPY",BODY,{"derivedFrom":makeQuery(id+"F15.opExtrude","SWEPT_BODY",BODY,{"disambiguationData":[OSD([sQuery(id+"F14.wireOp",EDGE,"E123"),sQuery(id+"F14.wireOp",EDGE,"E124"),sQuery(id+"F14.wireOp",EDGE,"E125"),sQuery(id+"F14.wireOp",EDGE,"E126"),sQuery(id+"F14.wireOp",EDGE,"E127"),sQuery(id+"F14.wireOp",EDGE,"E128"),sQuery(id+"F14.wireOp",EDGE,"E129")])]}),"instanceName":"1"});
            var Q7;
            Q7=makeQuery(id+"F21.opExtrude","SWEPT_BODY",BODY,{"disambiguationData":[OSD([sQuery(id+"F20.wireOp",EDGE,"E133"),sQuery(id+"F20.wireOp",EDGE,"E134")])]});
            var Q8;
            Q8=qCreatedBy(id+"F19.planeOp",FACE);
            mirror(context, id + "F22", {"entities" : qUnion([Q0, Q1, Q2, Q3, Q4, Q5, Q6, Q7]), "mirrorPlane" : qUnion([Q8])});
        }
        {
            var Q0;
            Q0=qCreatedBy(id+"F19.planeOp",FACE);
            var sketch = newSketch(context, id + "F23", { "sketchPlane" : qUnion([Q0])});
            skCircle(sketch, "E135", {"center": v(-393.13, 1025) * mm, "radius": 5.9 * mm});
            skSolve(sketch);
        }
        {
            var Q0;
            Q0=qSketchRegion(id+"F23",true);
            extrude(context, id + "F24", {"entities" : qUnion([Q0]), "endBound" : BoundingType.SYMMETRIC, "depth" : 770 * mm, "offsetDistance" : 25 * mm});
        }
        {
            var Q0;
            Q0=qCreatedBy(id+"F19.planeOp",FACE);
            var sketch = newSketch(context, id + "F25", { "sketchPlane" : qUnion([Q0])});
            skCircle(sketch, "E136", {"center": v(-393.13, 1025) * mm, "radius": 30 * mm});
            skCircle(sketch, "E137", {"center": v(-393.13, 1025) * mm, "radius": 6.25 * mm});
            skSolve(sketch);
        }
        {
            var Q0;
            Q0=qSketchRegion(id+"F25",true);
            extrude(context, id + "F26", {"entities" : qUnion([Q0]), "endBound" : BoundingType.SYMMETRIC, "depth" : 585 * mm, "offsetDistance" : 25 * mm});
        }
        {
            var Q0;
            Q0=makeQuery(id+"F24.opExtrude","CAP_EDGE",EDGE,{"disambiguationData":[OSD([sQuery(id+"F23.wireOp",EDGE,"E135")])],"isStart":true});
            var Q1;
            Q1=makeQuery(id+"F24.opExtrude","CAP_EDGE",EDGE,{"disambiguationData":[OSD([sQuery(id+"F23.wireOp",EDGE,"E135")])],"isStart":false});
            chamfer(context, id + "F27", {"entities" : qUnion([Q0, Q1]), "width" : 2 * mm, "tangentPropagation" : true});
        }
        {
            var Q0;
            Q0=makeQuery(id+"F26.opExtrude","CAP_EDGE",EDGE,{"disambiguationData":[OSD([sQuery(id+"F25.wireOp",EDGE,"E136")])],"isStart":false});
            var Q1;
            Q1=makeQuery(id+"F26.opExtrude","CAP_EDGE",EDGE,{"disambiguationData":[OSD([sQuery(id+"F25.wireOp",EDGE,"E136")])],"isStart":true});
            chamfer(context, id + "F28", {"entities" : qUnion([Q0, Q1]), "width" : 5 * mm, "tangentPropagation" : true});
        }
        {
            var Q0;
            Q0=makeQuery(id+"F26.opExtrude","SWEPT_FACE",FACE,{"disambiguationData":[OSD([sQuery(id+"F25.wireOp",EDGE,"E136")])]});
            cPlane(context, id + "F29", {"entities" : qUnion([Q0]), "cplaneType" : CPlaneType.LINE_ANGLE, "offset" : 25 * mm, "angle" : 0 * degree, "width" : 150 * mm, "height" : 150 * mm});
        }
        {
            var Q0;
            {var subQ0=sQuery(id+"F0.wireOp",EDGE,"E0");Q0=makeQuery(id+"F4.boolean.opBoolean","SPLIT",FACE,{"disambiguationData":[TD([makeQuery(id+"F4.opExtrude","SWEPT_FACE",FACE,{"disambiguationData":[OSD([sQuery(id+"F3.wireOp",EDGE,"E20.MirrorCS")])]})])],"derivedFrom":makeQuery(id+"F1.opExtrude","SWEPT_FACE",FACE,{"disambiguationData":[OSD([subQ0])]})});}
            var sketch = newSketch(context, id + "F30", { "sketchPlane" : qUnion([Q0])});
            skLineSegment(sketch, "E138", {"start": v(0, 220) * mm, "end": v(0, 180) * mm});
            skLineSegment(sketch, "E139", {"start": v(-720, 180) * mm, "end": v(0, 180) * mm});
            skLineSegment(sketch, "E140", {"start": v(-720, 180) * mm, "end": v(-720, 220) * mm});
            skLineSegment(sketch, "E141", {"start": v(0, 220) * mm, "end": v(-720, 220) * mm});
            skLineSegment(sketch, "E142", {"start": v(-720, 200) * mm, "end": v(0, 200) * mm, "construction": true});
            skCircle(sketch, "E143", {"center": v(-30, 200) * mm, "radius": 6.25 * mm});
            skCircle(sketch, "E144", {"center": v(-690, 200) * mm, "radius": 6.25 * mm});
            skLineSegment(sketch, "E145", {"start": v(-720, 645) * mm, "end": v(-720, 605) * mm});
            skLineSegment(sketch, "E146", {"start": v(-720, 605) * mm, "end": v(0, 605) * mm});
            skLineSegment(sketch, "E147", {"start": v(0, 605) * mm, "end": v(0, 645) * mm});
            skLineSegment(sketch, "E148", {"start": v(0, 645) * mm, "end": v(-720, 645) * mm});
            skLineSegment(sketch, "E149", {"start": v(-720, 625) * mm, "end": v(0, 625) * mm, "construction": true});
            skCircle(sketch, "E150", {"center": v(-690, 625) * mm, "radius": 6.25 * mm});
            skCircle(sketch, "E151", {"center": v(-30, 625) * mm, "radius": 6.25 * mm});
            skSolve(sketch);
        }
        {
            var Q0;
            Q0=qSketchRegion(id+"F30",true);
            extrude(context, id + "F31", {"entities" : qUnion([Q0]), "depth" : 4 * mm, "offsetDistance" : 25 * mm});
        }
        {
            var Q0;
            Q0=makeQuery(id+"F31.opExtrude","SWEPT_EDGE",EDGE,{"disambiguationData":[OSD([sQuery(id+"F30.wireOp",EDGE,"E138"),sQuery(id+"F30.wireOp",EDGE,"E141")])]});
            var Q1;
            Q1=makeQuery(id+"F31.opExtrude","SWEPT_EDGE",EDGE,{"disambiguationData":[OSD([sQuery(id+"F30.wireOp",EDGE,"E138"),sQuery(id+"F30.wireOp",EDGE,"E139")])]});
            var Q2;
            Q2=makeQuery(id+"F31.opExtrude","SWEPT_EDGE",EDGE,{"disambiguationData":[OSD([sQuery(id+"F30.wireOp",EDGE,"E140"),sQuery(id+"F30.wireOp",EDGE,"E141")])]});
            var Q3;
            Q3=makeQuery(id+"F31.opExtrude","SWEPT_EDGE",EDGE,{"disambiguationData":[OSD([sQuery(id+"F30.wireOp",EDGE,"E139"),sQuery(id+"F30.wireOp",EDGE,"E140")])]});
            var Q4;
            Q4=makeQuery(id+"F31.opExtrude","SWEPT_EDGE",EDGE,{"disambiguationData":[OSD([sQuery(id+"F30.wireOp",EDGE,"E145"),sQuery(id+"F30.wireOp",EDGE,"E148")])]});
            var Q5;
            Q5=makeQuery(id+"F31.opExtrude","SWEPT_EDGE",EDGE,{"disambiguationData":[OSD([sQuery(id+"F30.wireOp",EDGE,"E145"),sQuery(id+"F30.wireOp",EDGE,"E146")])]});
            var Q6;
            Q6=makeQuery(id+"F31.opExtrude","SWEPT_EDGE",EDGE,{"disambiguationData":[OSD([sQuery(id+"F30.wireOp",EDGE,"E147"),sQuery(id+"F30.wireOp",EDGE,"E148")])]});
            var Q7;
            Q7=makeQuery(id+"F31.opExtrude","SWEPT_EDGE",EDGE,{"disambiguationData":[OSD([sQuery(id+"F30.wireOp",EDGE,"E146"),sQuery(id+"F30.wireOp",EDGE,"E147")])]});
            fillet(context, id + "F32", {"entities" : qUnion([Q0, Q1, Q2, Q3, Q4, Q5, Q6, Q7]), "radius" : 7.5 * mm, "tangentPropagation" : true, "allowEdgeOverflow" : false});
        }
        {
            var Q0;
            Q0=makeQuery(id+"F31.opExtrude","SWEPT_BODY",BODY,{"disambiguationData":[OSD([sQuery(id+"F30.wireOp",EDGE,"E138"),sQuery(id+"F30.wireOp",EDGE,"E139"),sQuery(id+"F30.wireOp",EDGE,"E140"),sQuery(id+"F30.wireOp",EDGE,"E141"),sQuery(id+"F30.wireOp",EDGE,"E143"),sQuery(id+"F30.wireOp",EDGE,"E144")])]});
            var Q1;
            Q1=makeQuery(id+"F31.opExtrude","SWEPT_BODY",BODY,{"disambiguationData":[OSD([sQuery(id+"F30.wireOp",EDGE,"E145"),sQuery(id+"F30.wireOp",EDGE,"E146"),sQuery(id+"F30.wireOp",EDGE,"E147"),sQuery(id+"F30.wireOp",EDGE,"E148"),sQuery(id+"F30.wireOp",EDGE,"E150"),sQuery(id+"F30.wireOp",EDGE,"E151")])]});
            var Q2;
            Q2=qCreatedBy(id+"F12.planeOp",FACE);
            mirror(context, id + "F33", {"entities" : qUnion([Q0, Q1]), "mirrorPlane" : qUnion([Q2])});
        }
    });
